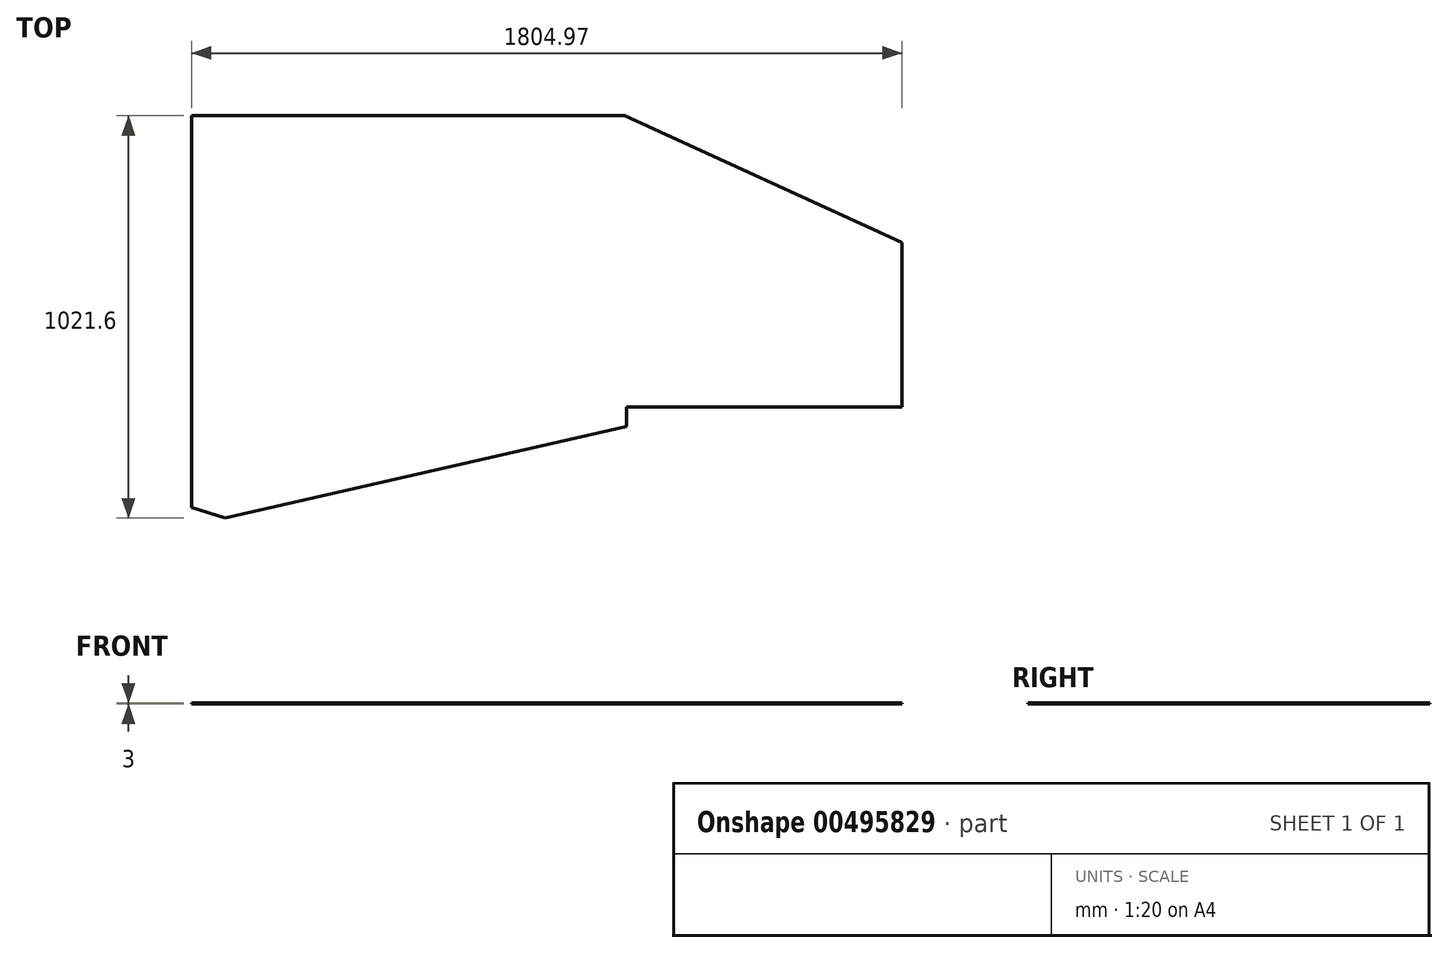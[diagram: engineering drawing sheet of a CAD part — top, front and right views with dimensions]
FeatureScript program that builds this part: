
annotation { "Feature Type Name" : "Feature", "Feature Type Description" : "" }
export const myFeature = defineFeature(function(context is Context, id is Id, definition is map)
    precondition{}
    {
        {
            var Q0;
            Q0=qCreatedBy(makeId("Top.planeOp"),FACE);
            var sketch = newSketch(context, id + "F0", { "sketchPlane" : qUnion([Q0])});
            skLineSegment(sketch, "E0", {"start": v(-1100, 0) * mm, "end": v(0, 0) * mm});
            skLineSegment(sketch, "E1", {"start": v(-1100, 0) * mm, "end": v(-1100, -995) * mm});
            skLineSegment(sketch, "E2", {"start": v(-1100, -995) * mm, "end": v(-1014.02, -1021.6) * mm});
            skLineSegment(sketch, "E3", {"start": v(-1014.02, -1021.6) * mm, "end": v(4.97, -789.93) * mm});
            skLineSegment(sketch, "E4", {"start": v(4.97, -789.93) * mm, "end": v(4.97, -739.93) * mm});
            skLineSegment(sketch, "E5", {"start": v(4.97, -739.93) * mm, "end": v(704.97, -739.93) * mm});
            skLineSegment(sketch, "E6", {"start": v(704.97, -739.93) * mm, "end": v(704.97, -321.93) * mm});
            skLineSegment(sketch, "E7", {"start": v(704.97, -321.93) * mm, "end": v(0, 0) * mm});
            skSolve(sketch);
        }
        {
            var Q0;
            Q0=makeQuery(id+"F0.imprint","IMPRINT",FACE,{"disambiguationData":[TD([[makeQuery(id+"F0.imprint","IMPRINT",EDGE,{"derivedFrom":sQuery(id+"F0.wireOp",EDGE,"E0")}),-1.0]])]});
            extrude(context, id + "F1", {"entities" : qUnion([Q0]), "depth" : 3 * mm});
        }
    });
